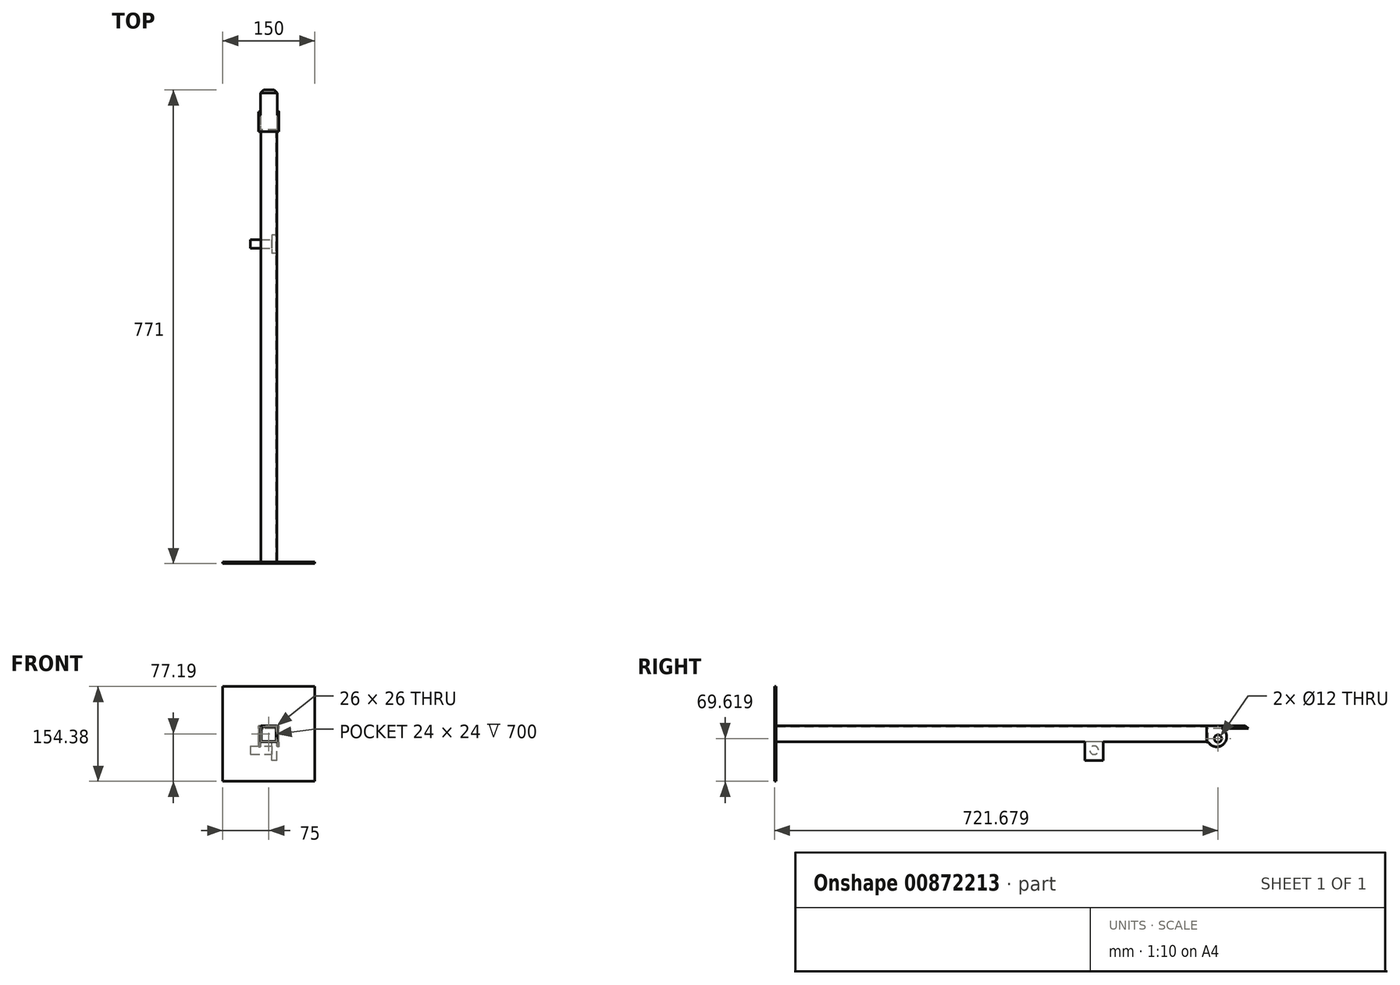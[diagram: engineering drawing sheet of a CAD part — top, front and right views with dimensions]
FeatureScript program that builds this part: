
annotation { "Feature Type Name" : "Feature", "Feature Type Description" : "" }
export const myFeature = defineFeature(function(context is Context, id is Id, definition is map)
    precondition{}
    {
        {
            var Q0;
            Q0=qCreatedBy(makeId("Front.planeOp"),FACE);
            var sketch = newSketch(context, id + "F0", { "sketchPlane" : qUnion([Q0])});
            skLineSegment(sketch, "E0.bottom", {"start": v(12, 12) * mm, "end": v(-12, 12) * mm});
            skLineSegment(sketch, "E0.top", {"start": v(12, -12) * mm, "end": v(-12, -12) * mm});
            skLineSegment(sketch, "E0.left", {"start": v(12, 12) * mm, "end": v(12, -12) * mm});
            skLineSegment(sketch, "E0.right", {"start": v(-12, 12) * mm, "end": v(-12, -12) * mm});
            skPoint(sketch, "E0.middle", {"position": v(0, 0) * mm});
            skLineSegment(sketch, "E1.bottom", {"start": v(13, 13) * mm, "end": v(-13, 13) * mm});
            skLineSegment(sketch, "E1.top", {"start": v(13, -13) * mm, "end": v(-13, -13) * mm});
            skLineSegment(sketch, "E1.left", {"start": v(13, 13) * mm, "end": v(13, -13) * mm});
            skLineSegment(sketch, "E1.right", {"start": v(-13, 13) * mm, "end": v(-13, -13) * mm});
            skSolve(sketch);
        }
        {
            var Q0;
            Q0=makeQuery(id+"F0.imprint","IMPRINT",FACE,{"disambiguationData":[TD([[makeQuery(id+"F0.imprint","IMPRINT",EDGE,{"derivedFrom":sQuery(id+"F0.wireOp",EDGE,"E0.bottom")}),-1.0]])]});
            extrude(context, id + "F1", {"entities" : qUnion([Q0]), "depth" : 700 * mm, "offsetDistance" : 25 * mm});
        }
        {
            var Q0;
            Q0=makeQuery(id+"F1.opExtrude","CAP_FACE",FACE,{"disambiguationData":[OSD([sQuery(id+"F0.wireOp",EDGE,"E0.bottom"),sQuery(id+"F0.wireOp",EDGE,"E0.top"),sQuery(id+"F0.wireOp",EDGE,"E0.left"),sQuery(id+"F0.wireOp",EDGE,"E0.right"),sQuery(id+"F0.wireOp",EDGE,"E1.bottom"),sQuery(id+"F0.wireOp",EDGE,"E1.top"),sQuery(id+"F0.wireOp",EDGE,"E1.left"),sQuery(id+"F0.wireOp",EDGE,"E1.right")])],"isStart":true});
            var sketch = newSketch(context, id + "F2", { "sketchPlane" : qUnion([Q0])});
            skLineSegment(sketch, "E2.bottom", {"start": v(-13.5, -13.5) * mm, "end": v(13.5, -13.5) * mm});
            skLineSegment(sketch, "E2.top", {"start": v(-13.5, 13.5) * mm, "end": v(13.5, 13.5) * mm});
            skLineSegment(sketch, "E2.left", {"start": v(-13.5, -13.5) * mm, "end": v(-13.5, 13.5) * mm});
            skLineSegment(sketch, "E2.right", {"start": v(13.5, -13.5) * mm, "end": v(13.5, 13.5) * mm});
            skPoint(sketch, "E2.middle", {"position": v(0, 0) * mm});
            skSolve(sketch);
        }
        {
            var Q0;
            Q0=makeQuery(id+"F2.imprint","IMPRINT",FACE,{"disambiguationData":[TD([[makeQuery(id+"F2.imprint","IMPRINT",EDGE,{"derivedFrom":sQuery(id+"F2.wireOp",EDGE,"E2.bottom")}),1.0]])]});
            var Q1;
            Q1=makeQuery(id+"F2.imprint","IMPRINT",FACE,{"disambiguationData":[TD([[makeQuery(id+"F2.imprint","IMPRINT",EDGE,{"derivedFrom":makeQuery(id+"F1.opExtrude","CAP_EDGE",EDGE,{"disambiguationData":[OSD([sQuery(id+"F0.wireOp",EDGE,"E0.bottom")])],"isStart":true})}),1.0]])]});
            var Q2;
            Q2=makeQuery(id+"F2.imprint","IMPRINT",FACE,{"disambiguationData":[TD([[makeQuery(id+"F2.imprint","IMPRINT",EDGE,{"derivedFrom":makeQuery(id+"F1.opExtrude","CAP_EDGE",EDGE,{"disambiguationData":[OSD([sQuery(id+"F0.wireOp",EDGE,"E0.bottom")])],"isStart":true})}),-1.0]])]});
            extrude(context, id + "F3", {"entities" : qUnion([Q0, Q1, Q2]), "operationType" : NewBodyOperationType.ADD, "depth" : 3 * mm, "offsetDistance" : 25 * mm});
        }
        {
            var Q0;
            Q0=makeQuery(id+"F1.opExtrude","CAP_FACE",FACE,{"disambiguationData":[OSD([sQuery(id+"F0.wireOp",EDGE,"E0.bottom"),sQuery(id+"F0.wireOp",EDGE,"E0.top"),sQuery(id+"F0.wireOp",EDGE,"E0.left"),sQuery(id+"F0.wireOp",EDGE,"E0.right"),sQuery(id+"F0.wireOp",EDGE,"E1.bottom"),sQuery(id+"F0.wireOp",EDGE,"E1.top"),sQuery(id+"F0.wireOp",EDGE,"E1.left"),sQuery(id+"F0.wireOp",EDGE,"E1.right")])],"isStart":false});
            var sketch = newSketch(context, id + "F4", { "sketchPlane" : qUnion([Q0])});
            skLineSegment(sketch, "E3.bottom", {"start": v(75, 77.2) * mm, "end": v(-75, 77.2) * mm});
            skLineSegment(sketch, "E3.top", {"start": v(75, -77.2) * mm, "end": v(-75, -77.2) * mm});
            skLineSegment(sketch, "E3.left", {"start": v(75, 77.2) * mm, "end": v(75, -77.2) * mm});
            skLineSegment(sketch, "E3.right", {"start": v(-75, 77.2) * mm, "end": v(-75, -77.2) * mm});
            skPoint(sketch, "E3.middle", {"position": v(0, 0) * mm});
            skSolve(sketch);
        }
        {
            var Q0;
            Q0=makeQuery(id+"F4.imprint","IMPRINT",FACE,{"disambiguationData":[TD([[makeQuery(id+"F4.imprint","IMPRINT",EDGE,{"derivedFrom":sQuery(id+"F4.wireOp",EDGE,"E3.bottom")}),1.0]])]});
            extrude(context, id + "F5", {"entities" : qUnion([Q0]), "depth" : 3 * mm, "offsetDistance" : 25 * mm});
        }
        {
            var Q0;
            Q0=makeQuery(id+"F3.opExtrude","CAP_FACE",FACE,{"disambiguationData":[OSD([sQuery(id+"F2.wireOp",EDGE,"E2.bottom"),sQuery(id+"F2.wireOp",EDGE,"E2.top"),sQuery(id+"F2.wireOp",EDGE,"E2.left"),sQuery(id+"F2.wireOp",EDGE,"E2.right")])],"isStart":false});
            var sketch = newSketch(context, id + "F6", { "sketchPlane" : qUnion([Q0])});
            skLineSegment(sketch, "E4.bottom", {"start": v(-13.5, 13.5) * mm, "end": v(13.5, 13.5) * mm});
            skLineSegment(sketch, "E4.top", {"start": v(-13.5, 8.5) * mm, "end": v(13.5, 8.5) * mm});
            skLineSegment(sketch, "E4.left", {"start": v(-13.5, 13.5) * mm, "end": v(-13.5, 8.5) * mm});
            skLineSegment(sketch, "E4.right", {"start": v(13.5, 13.5) * mm, "end": v(13.5, 8.5) * mm});
            skSolve(sketch);
        }
        {
            var Q0;
            Q0=makeQuery(id+"F6.imprint","IMPRINT",FACE,{"disambiguationData":[TD([[makeQuery(id+"F6.imprint","IMPRINT",EDGE,{"derivedFrom":sQuery(id+"F6.wireOp",EDGE,"E4.bottom")}),-1.0]])]});
            extrude(context, id + "F7", {"entities" : qUnion([Q0]), "operationType" : NewBodyOperationType.ADD, "depth" : 65 * mm, "offsetDistance" : 25 * mm});
        }
        {
            var Q0;
            Q0=makeQuery(id+"F7.opExtrude","CAP_EDGE",EDGE,{"disambiguationData":[OSD([sQuery(id+"F6.wireOp",EDGE,"E4.left")])],"isStart":false});
            var Q1;
            Q1=makeQuery(id+"F7.opExtrude","CAP_EDGE",EDGE,{"disambiguationData":[OSD([sQuery(id+"F6.wireOp",EDGE,"E4.bottom")])],"isStart":false});
            var Q2;
            Q2=makeQuery(id+"F7.opExtrude","CAP_EDGE",EDGE,{"disambiguationData":[OSD([sQuery(id+"F6.wireOp",EDGE,"E4.right")])],"isStart":false});
            chamfer(context, id + "F8", {"entities" : qUnion([Q0, Q1, Q2]), "width" : 5 * mm, "tangentPropagation" : true});
        }
        {
            var Q0;
            Q0=makeQuery(id+"F7.boolean.opBoolean","MERGE",FACE,{"derivedFrom":[makeQuery(id+"F3.opExtrude","SWEPT_FACE",FACE,{"disambiguationData":[OSD([sQuery(id+"F2.wireOp",EDGE,"E2.left")])]}),makeQuery(id+"F7.opExtrude","SWEPT_FACE",FACE,{"disambiguationData":[OSD([sQuery(id+"F6.wireOp",EDGE,"E4.left")])]})]});
            var sketch = newSketch(context, id + "F9", { "sketchPlane" : qUnion([Q0])});
            skArc(sketch, "E5", {"start": v(3, -13.5) * mm, "mid": v(27.8, -16.42) * mm, "end": v(26.06, 8.5) * mm});
            skLineSegment(sketch, "E6", {"start": v(3, -13.5) * mm, "end": v(0, -13.5) * mm});
            skLineSegment(sketch, "E7", {"start": v(0, -13.5) * mm, "end": v(0, 13.5) * mm});
            skLineSegment(sketch, "E8", {"start": v(0, 13.5) * mm, "end": v(26.81, 13.5) * mm});
            skLineSegment(sketch, "E9", {"start": v(26.81, 13.5) * mm, "end": v(26.06, 8.5) * mm});
            skSolve(sketch);
        }
        {
            var Q0;
            Q0=makeQuery(id+"F9.imprint","IMPRINT",FACE,{"disambiguationData":[TD([[makeQuery(id+"F9.imprint","IMPRINT",EDGE,{"derivedFrom":sQuery(id+"F9.wireOp",EDGE,"E6")}),-1.0]])]});
            var Q1;
            {var subQ0=sQuery(id+"F9.wireOp",EDGE,"E5");Q1=makeQuery(id+"F9.imprint","IMPRINT",FACE,{"disambiguationData":[TD([[makeQuery(id+"F9.imprint","IMPRINT",EDGE,{"derivedFrom":subQ0}),1.0]])]});}
            extrude(context, id + "F10", {"entities" : qUnion([Q0, Q1]), "operationType" : NewBodyOperationType.ADD, "depth" : 3 * mm, "offsetDistance" : 25 * mm});
        }
        {
            var Q0;
            Q0=makeQuery(id+"F7.boolean.opBoolean","MERGE",FACE,{"derivedFrom":[makeQuery(id+"F3.opExtrude","SWEPT_FACE",FACE,{"disambiguationData":[OSD([sQuery(id+"F2.wireOp",EDGE,"E2.right")])]}),makeQuery(id+"F7.opExtrude","SWEPT_FACE",FACE,{"disambiguationData":[OSD([sQuery(id+"F6.wireOp",EDGE,"E4.right")])]})]});
            var sketch = newSketch(context, id + "F11", { "sketchPlane" : qUnion([Q0])});
            skArc(sketch, "E10", {"start": v(-25.78, 8.5) * mm, "mid": v(-27.9, -16.48) * mm, "end": v(-3, -13.5) * mm});
            skLineSegment(sketch, "E11", {"start": v(-25.78, 8.5) * mm, "end": v(-27.06, 13.5) * mm});
            skLineSegment(sketch, "E12", {"start": v(-27.06, 13.5) * mm, "end": v(0, 13.5) * mm});
            skLineSegment(sketch, "E13", {"start": v(0, 13.5) * mm, "end": v(0, -13.5) * mm});
            skLineSegment(sketch, "E14", {"start": v(0, -13.5) * mm, "end": v(-3, -13.5) * mm});
            skSolve(sketch);
        }
        {
            var Q0;
            {var subQ0=sQuery(id+"F11.wireOp",EDGE,"E11");Q0=makeQuery(id+"F11.imprint","IMPRINT",FACE,{"disambiguationData":[TD([[makeQuery(id+"F11.imprint","IMPRINT",EDGE,{"derivedFrom":subQ0}),-1.0]])]});}
            var Q1;
            {var subQ0=sQuery(id+"F11.wireOp",EDGE,"E10");Q1=makeQuery(id+"F11.imprint","IMPRINT",FACE,{"disambiguationData":[TD([[makeQuery(id+"F11.imprint","IMPRINT",EDGE,{"derivedFrom":subQ0}),1.0]])]});}
            extrude(context, id + "F12", {"entities" : qUnion([Q0, Q1]), "operationType" : NewBodyOperationType.ADD, "depth" : 3 * mm, "offsetDistance" : 25 * mm});
        }
        {
            var Q0;
            Q0=makeQuery(id+"F10.opExtrude","CAP_FACE",FACE,{"disambiguationData":[OSD([sQuery(id+"F9.wireOp",EDGE,"E5"),sQuery(id+"F9.wireOp",EDGE,"E6"),sQuery(id+"F9.wireOp",EDGE,"E7"),sQuery(id+"F9.wireOp",EDGE,"E8"),sQuery(id+"F9.wireOp",EDGE,"E9")])],"isStart":false});
            var sketch = newSketch(context, id + "F13", { "sketchPlane" : qUnion([Q0])});
            skCircle(sketch, "E15", {"center": v(18.68, -7.57) * mm, "radius": 6.1 * mm});
            skSolve(sketch);
        }
        {
            var Q0;
            Q0=sQuery(id+"F13.wireOp",VERTEX,"E15.center");
            var Q1;
            Q1=makeQuery(id+"F1.opExtrude","SWEPT_BODY",BODY,{"disambiguationData":[OSD([sQuery(id+"F0.wireOp",EDGE,"E0.bottom"),sQuery(id+"F0.wireOp",EDGE,"E0.top"),sQuery(id+"F0.wireOp",EDGE,"E0.left"),sQuery(id+"F0.wireOp",EDGE,"E0.right"),sQuery(id+"F0.wireOp",EDGE,"E1.bottom"),sQuery(id+"F0.wireOp",EDGE,"E1.top"),sQuery(id+"F0.wireOp",EDGE,"E1.left"),sQuery(id+"F0.wireOp",EDGE,"E1.right")])]});
            hole(context, id + "F14", {"style" : HoleStyle.SIMPLE, "endStyle" : HoleEndStyle.THROUGH, "holeDiameter" : 12 * mm, "majorDiameter" : 5 * mm, "isTappedThrough" : true, "tappedDepth" : 12 * mm, "tapClearance" : 3, "locations" : qUnion([Q0]), "scope" : qUnion([Q1])});
        }
        {
            var Q0;
            Q0=makeQuery(id+"F1.opExtrude","SWEPT_FACE",FACE,{"disambiguationData":[OSD([sQuery(id+"F0.wireOp",EDGE,"E1.top")])]});
            var sketch = newSketch(context, id + "F15", { "sketchPlane" : qUnion([Q0])});
            skLineSegment(sketch, "E16.bottom", {"start": v(13, 167.9) * mm, "end": v(5, 167.9) * mm});
            skLineSegment(sketch, "E16.top", {"start": v(13, 197.9) * mm, "end": v(5, 197.9) * mm});
            skLineSegment(sketch, "E16.left", {"start": v(13, 167.9) * mm, "end": v(13, 197.9) * mm});
            skLineSegment(sketch, "E16.right", {"start": v(5, 167.9) * mm, "end": v(5, 197.9) * mm});
            skSolve(sketch);
        }
        {
            var Q0;
            Q0=makeQuery(id+"F15.imprint","IMPRINT",FACE,{"disambiguationData":[TD([[makeQuery(id+"F15.imprint","IMPRINT",EDGE,{"derivedFrom":sQuery(id+"F15.wireOp",EDGE,"E16.bottom")}),-1.0]])]});
            extrude(context, id + "F16", {"entities" : qUnion([Q0]), "operationType" : NewBodyOperationType.ADD, "depth" : 30 * mm, "offsetDistance" : 25 * mm});
        }
        {
            var Q0;
            Q0=makeQuery(id+"F16.opExtrude","SWEPT_FACE",FACE,{"disambiguationData":[OSD([sQuery(id+"F15.wireOp",EDGE,"E16.right")])]});
            var sketch = newSketch(context, id + "F17", { "sketchPlane" : qUnion([Q0])});
            skCircle(sketch, "E17", {"center": v(182.9, -26.45) * mm, "radius": 6.94 * mm});
            skPoint(sketch, "E17.centerSnap0", {"position": v(182.9, -43) * mm});
            skSolve(sketch);
        }
        {
            var Q0;
            Q0 = qSketchRegion(id + "F17", true);
            extrude(context, id + "F18", {"entities" : qUnion([Q0]), "operationType" : NewBodyOperationType.ADD, "depth" : 35 * mm, "offsetDistance" : 25 * mm});
        }
    });
